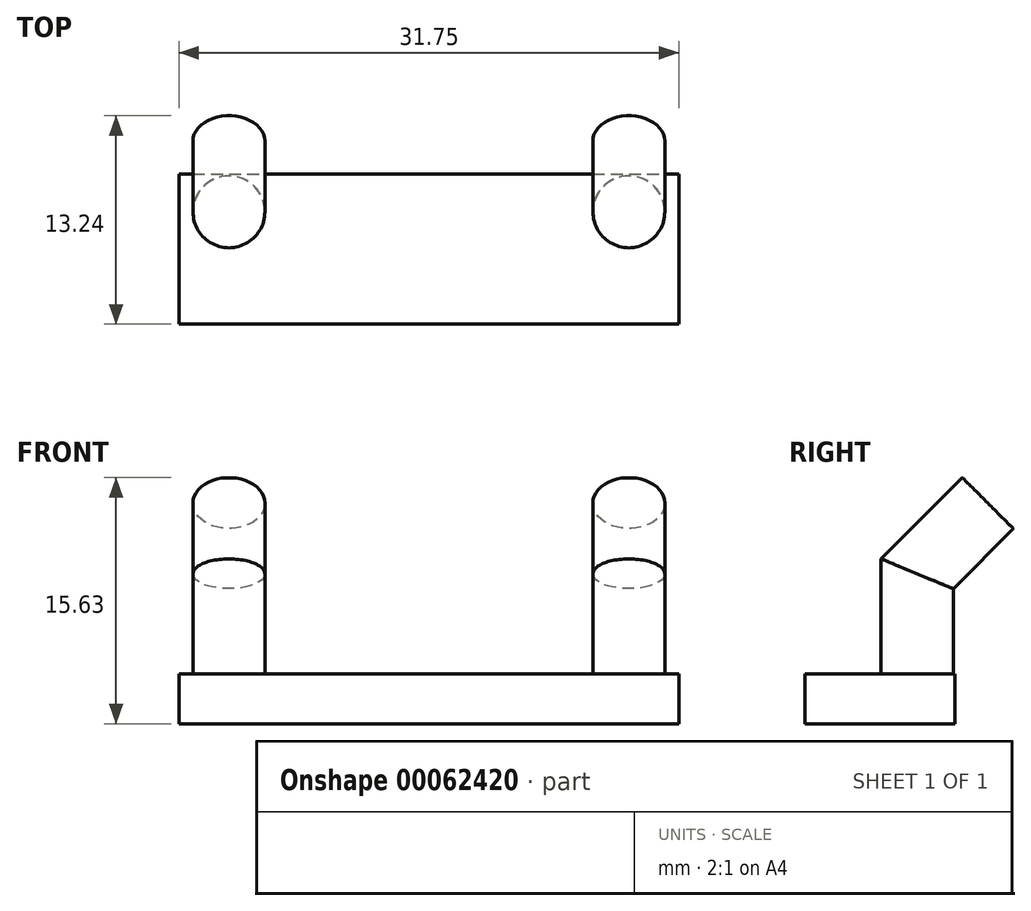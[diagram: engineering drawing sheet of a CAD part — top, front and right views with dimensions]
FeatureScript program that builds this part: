
annotation { "Feature Type Name" : "Feature", "Feature Type Description" : "" }
export const myFeature = defineFeature(function(context is Context, id is Id, definition is map)
    precondition{}
    {
        {
            var Q0;
            Q0=qCreatedBy(makeId("Top.planeOp"),FACE);
            var sketch = newSketch(context, id + "F0", { "sketchPlane" : qUnion([Q0])});
            skLineSegment(sketch, "E0.bottom", {"start": v(0, 0) * mm, "end": v(31.75, 0) * mm});
            skLineSegment(sketch, "E0.top", {"start": v(0, 9.52) * mm, "end": v(31.75, 9.52) * mm});
            skLineSegment(sketch, "E0.left", {"start": v(0, 0) * mm, "end": v(0, 9.52) * mm});
            skLineSegment(sketch, "E0.right", {"start": v(31.75, 0) * mm, "end": v(31.75, 9.52) * mm});
            skSolve(sketch);
        }
        {
            var Q0;
            Q0=makeQuery(id+"F0.imprint","IMPRINT",FACE,{"disambiguationData":[TD([[makeQuery(id+"F0.imprint","IMPRINT",EDGE,{"derivedFrom":sQuery(id+"F0.wireOp",EDGE,"E0.bottom")}),1.0]])]});
            extrude(context, id + "F1", {"entities" : qUnion([Q0]), "depth" : 3.17 * mm});
        }
        {
            var Q0;
            Q0=makeQuery(id+"F1.opExtrude","SWEPT_FACE",FACE,{"disambiguationData":[OSD([sQuery(id+"F0.wireOp",EDGE,"E0.right")])]});
            cPlane(context, id + "F2", {"entities" : qUnion([Q0]), "cplaneType" : CPlaneType.OFFSET, "offset" : 3.17 * mm, "oppositeDirection" : true, "width" : 152.4 * mm, "height" : 152.4 * mm});
        }
        {
            var Q0;
            Q0=qCreatedBy(id+"F2.planeOp",FACE);
            var sketch = newSketch(context, id + "F3", { "sketchPlane" : qUnion([Q0])});
            skLineSegment(sketch, "E1", {"start": v(7.14, 3.18) * mm, "end": v(7.14, 9.53) * mm});
            skLineSegment(sketch, "E2", {"start": v(7.14, 9.53) * mm, "end": v(11.63, 14.02) * mm});
            skSolve(sketch);
        }
        {
            var Q0;
            Q0=makeQuery(id+"F1.opExtrude","CAP_FACE",FACE,{"disambiguationData":[OSD([sQuery(id+"F0.wireOp",EDGE,"E0.bottom"),sQuery(id+"F0.wireOp",EDGE,"E0.top"),sQuery(id+"F0.wireOp",EDGE,"E0.left"),sQuery(id+"F0.wireOp",EDGE,"E0.right")])],"isStart":false});
            var sketch = newSketch(context, id + "F4", { "sketchPlane" : qUnion([Q0])});
            skCircle(sketch, "E3", {"center": v(28.57, 7.14) * mm, "radius": 2.29 * mm});
            skSolve(sketch);
        }
        {
            var Q0;
            Q0=makeQuery(id+"F4.imprint","IMPRINT",FACE,{"disambiguationData":[TD([[makeQuery(id+"F4.imprint","IMPRINT",EDGE,{"derivedFrom":sQuery(id+"F4.wireOp",EDGE,"E3")}),1.0]])]});
            var Q1;
            Q1=sQuery(id+"F3.wireOp",EDGE,"E1");
            var Q2;
            Q2=sQuery(id+"F3.wireOp",EDGE,"E2");
            sweep(context, id + "F5", {"operationType" : NewBodyOperationType.ADD, "profiles" : qUnion([Q0]), "path" : qUnion([Q1, Q2])});
        }
        {
            var Q0;
            Q0=qCreatedBy(id+"F2.planeOp",FACE);
            cPlane(context, id + "F6", {"entities" : qUnion([Q0]), "cplaneType" : CPlaneType.OFFSET, "offset" : 25.4 * mm, "oppositeDirection" : true, "width" : 152.4 * mm, "height" : 152.4 * mm});
        }
        {
            var Q0;
            Q0=qCreatedBy(id+"F6.planeOp",FACE);
            var sketch = newSketch(context, id + "F7", { "sketchPlane" : qUnion([Q0])});
            skLineSegment(sketch, "E4.0", {"start": v(7.14, 3.18) * mm, "end": v(7.14, 9.53) * mm});
            skLineSegment(sketch, "E4.1", {"start": v(7.14, 9.53) * mm, "end": v(11.63, 14.02) * mm});
            skSolve(sketch);
        }
        {
            var Q0;
            Q0=makeQuery(id+"F1.opExtrude","CAP_FACE",FACE,{"disambiguationData":[OSD([sQuery(id+"F0.wireOp",EDGE,"E0.bottom"),sQuery(id+"F0.wireOp",EDGE,"E0.top"),sQuery(id+"F0.wireOp",EDGE,"E0.left"),sQuery(id+"F0.wireOp",EDGE,"E0.right")])],"isStart":false});
            var sketch = newSketch(context, id + "F8", { "sketchPlane" : qUnion([Q0])});
            skCircle(sketch, "E5", {"center": v(3.17, 7.14) * mm, "radius": 2.29 * mm});
            skSolve(sketch);
        }
        {
            var Q0;
            Q0=makeQuery(id+"F8.imprint","IMPRINT",FACE,{"disambiguationData":[TD([[makeQuery(id+"F8.imprint","IMPRINT",EDGE,{"derivedFrom":sQuery(id+"F8.wireOp",EDGE,"E5")}),1.0]])]});
            var Q1;
            Q1=sQuery(id+"F7.wireOp",EDGE,"E4.0");
            var Q2;
            Q2=sQuery(id+"F7.wireOp",EDGE,"E4.1");
            sweep(context, id + "F9", {"operationType" : NewBodyOperationType.ADD, "profiles" : qUnion([Q0]), "path" : qUnion([Q1, Q2])});
        }
    });
